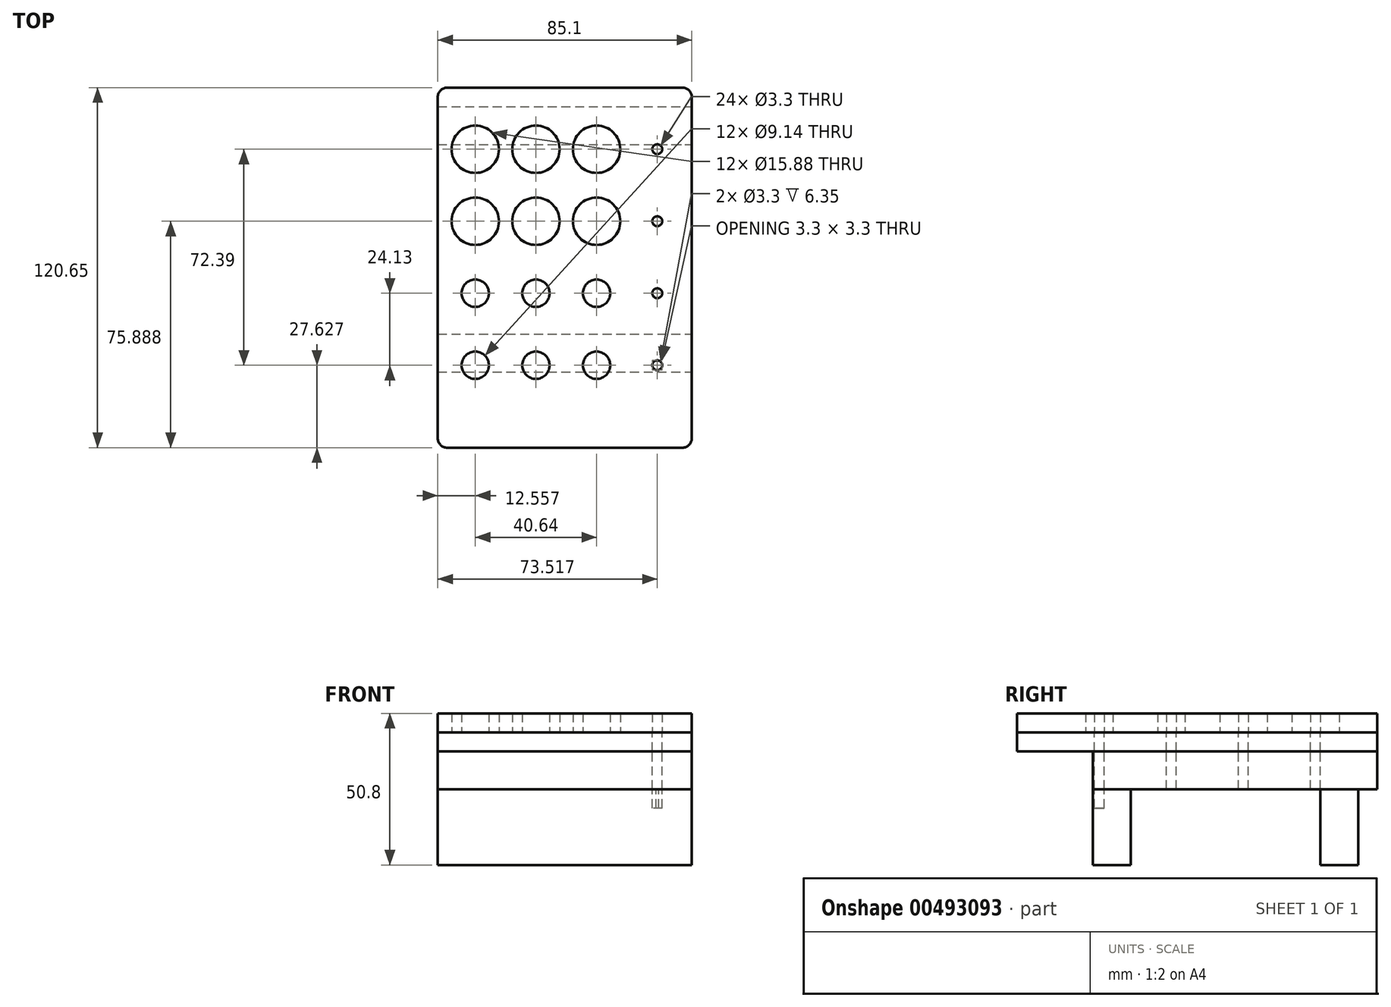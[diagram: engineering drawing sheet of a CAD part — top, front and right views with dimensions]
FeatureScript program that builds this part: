
annotation { "Feature Type Name" : "Feature", "Feature Type Description" : "" }
export const myFeature = defineFeature(function(context is Context, id is Id, definition is map)
    precondition{}
    {
        {
            var Q0;
            Q0=qCreatedBy(makeId("Top.planeOp"),FACE);
            var sketch = newSketch(context, id + "F0", { "sketchPlane" : qUnion([Q0])});
            skLineSegment(sketch, "E0.bottom", {"start": v(-42.55, 47.63) * mm, "end": v(42.55, 47.63) * mm});
            skLineSegment(sketch, "E0.top", {"start": v(-42.55, -47.63) * mm, "end": v(42.55, -47.63) * mm});
            skLineSegment(sketch, "E0.left", {"start": v(-42.55, 47.63) * mm, "end": v(-42.55, -47.63) * mm});
            skLineSegment(sketch, "E0.right", {"start": v(42.55, 47.63) * mm, "end": v(42.55, -47.63) * mm});
            skPoint(sketch, "E0.middle", {"position": v(0, 0) * mm});
            skSolve(sketch);
        }
        {
            var Q0;
            Q0=qSketchRegion(id+"F0",true);
            extrude(context, id + "F1", {"entities" : qUnion([Q0]), "depth" : 12.7 * mm});
        }
        {
            var Q0;
            Q0=makeQuery(id+"F1.opExtrude","CAP_FACE",FACE,{"disambiguationData":[OSD([sQuery(id+"F0.wireOp",EDGE,"E0.bottom"),sQuery(id+"F0.wireOp",EDGE,"E0.top"),sQuery(id+"F0.wireOp",EDGE,"E0.left"),sQuery(id+"F0.wireOp",EDGE,"E0.right")])],"isStart":false});
            var sketch = newSketch(context, id + "F2", { "sketchPlane" : qUnion([Q0])});
            skLineSegment(sketch, "E1", {"start": v(0, 47.63) * mm, "end": v(0, -47.63) * mm, "construction": true});
            skPoint(sketch, "E2", {"position": v(0, 41.28) * mm});
            skLineSegment(sketch, "E3.bottom", {"start": v(-42.55, 47.63) * mm, "end": v(42.55, 47.63) * mm});
            skLineSegment(sketch, "E3.top", {"start": v(-42.54, -73.03) * mm, "end": v(-36.2, -73.03) * mm});
            skLineSegment(sketch, "E3.left", {"start": v(-42.55, 47.62) * mm, "end": v(-42.55, -73.03) * mm});
            skLineSegment(sketch, "E3.right", {"start": v(42.55, 47.62) * mm, "end": v(42.55, -73.03) * mm});
            skLineSegment(sketch, "E4.trimOffspring", {"start": v(-21.97, -73.03) * mm, "end": v(-7.11, -73.03) * mm});
            skLineSegment(sketch, "E5.trimOffspring", {"start": v(7.11, -73.03) * mm, "end": v(21.97, -73.03) * mm});
            skLineSegment(sketch, "E6.trimOffspring", {"start": v(36.2, -73.03) * mm, "end": v(42.55, -73.03) * mm});
            skPoint(sketch, "E7.orphan", {"position": v(-36.2, -85.72) * mm});
            skPoint(sketch, "E8.MirrorCS.start.orphan", {"position": v(-21.97, -85.72) * mm});
            skPoint(sketch, "E9.orphan", {"position": v(7.11, -85.72) * mm});
            skPoint(sketch, "E10.top.start.orphan", {"position": v(21.97, -85.72) * mm});
            skPoint(sketch, "E11.orphan", {"position": v(36.2, -85.72) * mm});
            skLineSegment(sketch, "E12", {"start": v(-42.55, -73.03) * mm, "end": v(42.55, -73.03) * mm});
            skSolve(sketch);
        }
        {
            var Q0;
            Q0 = qSketchRegion(id + "F2", true);
            extrude(context, id + "F3", {"entities" : qUnion([Q0]), "depth" : 6.35 * mm});
        }
        {
            var Q0;
            Q0=makeQuery(id+"F1.opExtrude","CAP_FACE",FACE,{"disambiguationData":[OSD([sQuery(id+"F0.wireOp",EDGE,"E0.bottom"),sQuery(id+"F0.wireOp",EDGE,"E0.top"),sQuery(id+"F0.wireOp",EDGE,"E0.left"),sQuery(id+"F0.wireOp",EDGE,"E0.right")])],"isStart":true});
            var sketch = newSketch(context, id + "F4", { "sketchPlane" : qUnion([Q0])});
            skLineSegment(sketch, "E13.bottom", {"start": v(-42.55, 47.63) * mm, "end": v(42.55, 47.63) * mm});
            skLineSegment(sketch, "E13.top", {"start": v(-42.55, 34.93) * mm, "end": v(42.55, 34.93) * mm});
            skLineSegment(sketch, "E13.left", {"start": v(-42.55, 47.63) * mm, "end": v(-42.55, 34.93) * mm});
            skLineSegment(sketch, "E13.right", {"start": v(42.55, 47.63) * mm, "end": v(42.55, 34.93) * mm});
            skLineSegment(sketch, "E14.bottom", {"start": v(-42.55, -41.28) * mm, "end": v(42.55, -41.28) * mm});
            skLineSegment(sketch, "E14.top", {"start": v(-42.55, -28.58) * mm, "end": v(42.55, -28.58) * mm});
            skLineSegment(sketch, "E14.left", {"start": v(-42.55, -41.28) * mm, "end": v(-42.55, -28.58) * mm});
            skLineSegment(sketch, "E14.right", {"start": v(42.55, -41.28) * mm, "end": v(42.55, -28.58) * mm});
            skSolve(sketch);
        }
        {
            var Q0;
            Q0 = qSketchRegion(id + "F4", true);
            extrude(context, id + "F5", {"entities" : qUnion([Q0]), "depth" : 25.4 * mm});
        }
        {
            var Q0;
            Q0=makeQuery(id+"F3.opExtrude","CAP_FACE",FACE,{"disambiguationData":[OSD([sQuery(id+"F2.wireOp",EDGE,"E3.bottom"),sQuery(id+"F2.wireOp",EDGE,"E3.left"),sQuery(id+"F2.wireOp",EDGE,"E3.right"),sQuery(id+"F2.wireOp",EDGE,"E12")])],"isStart":false});
            var sketch = newSketch(context, id + "F6", { "sketchPlane" : qUnion([Q0])});
            skLineSegment(sketch, "E15.bottom", {"start": v(-42.55, 47.63) * mm, "end": v(42.55, 47.63) * mm});
            skLineSegment(sketch, "E15.top", {"start": v(-42.55, -73.03) * mm, "end": v(42.55, -73.03) * mm});
            skLineSegment(sketch, "E15.left", {"start": v(-42.55, 47.62) * mm, "end": v(-42.55, -73.03) * mm});
            skLineSegment(sketch, "E15.right", {"start": v(42.55, 47.62) * mm, "end": v(42.55, -73.03) * mm});
            skCircle(sketch, "E16", {"center": v(-30, 26.99) * mm, "radius": 7.94 * mm});
            skCircle(sketch, "E17.0.1.0", {"center": v(-30, 2.86) * mm, "radius": 7.94 * mm});
            skCircle(sketch, "E17.1.0.0", {"center": v(-9.67, 26.99) * mm, "radius": 7.94 * mm});
            skCircle(sketch, "E17.1.1.0", {"center": v(-9.67, 2.86) * mm, "radius": 7.94 * mm});
            skCircle(sketch, "E17.2.0.0", {"center": v(10.65, 26.99) * mm, "radius": 7.94 * mm});
            skCircle(sketch, "E17.2.1.0", {"center": v(10.65, 2.86) * mm, "radius": 7.94 * mm});
            skLineSegment(sketch, "E17.direction1", {"start": v(-30, 26.99) * mm, "end": v(-9.67, 26.99) * mm, "construction": true});
            skLineSegment(sketch, "E17.direction2", {"start": v(-30, 26.99) * mm, "end": v(-30, 2.86) * mm, "construction": true});
            skCircle(sketch, "E18.0.3.0", {"center": v(30.97, 26.99) * mm, "radius": 7.94 * mm, "construction": true});
            skCircle(sketch, "E18.0.3.1", {"center": v(30.97, 2.86) * mm, "radius": 7.94 * mm, "construction": true});
            skCircle(sketch, "E19", {"center": v(30.97, 26.99) * mm, "radius": 1.65 * mm});
            skCircle(sketch, "E20", {"center": v(30.97, 2.86) * mm, "radius": 1.65 * mm});
            skCircle(sketch, "E21.0.0.2", {"center": v(-30, -21.27) * mm, "radius": 7.94 * mm, "construction": true});
            skCircle(sketch, "E21.0.0.3", {"center": v(-30, -45.4) * mm, "radius": 7.94 * mm, "construction": true});
            skCircle(sketch, "E21.0.1.2", {"center": v(-9.67, -21.27) * mm, "radius": 7.94 * mm, "construction": true});
            skCircle(sketch, "E21.0.1.3", {"center": v(-9.67, -45.4) * mm, "radius": 7.94 * mm, "construction": true});
            skCircle(sketch, "E21.0.2.2", {"center": v(10.65, -21.27) * mm, "radius": 7.94 * mm, "construction": true});
            skCircle(sketch, "E21.0.2.3", {"center": v(10.65, -45.4) * mm, "radius": 7.94 * mm, "construction": true});
            skCircle(sketch, "E21.0.3.2", {"center": v(30.97, -21.27) * mm, "radius": 7.94 * mm, "construction": true});
            skCircle(sketch, "E21.0.3.3", {"center": v(30.97, -45.4) * mm, "radius": 7.94 * mm, "construction": true});
            skCircle(sketch, "E22", {"center": v(-30, -21.27) * mm, "radius": 4.57 * mm});
            skCircle(sketch, "E23", {"center": v(-9.67, -21.27) * mm, "radius": 4.57 * mm});
            skCircle(sketch, "E24", {"center": v(10.65, -21.27) * mm, "radius": 4.57 * mm});
            skCircle(sketch, "E25", {"center": v(30.97, -21.27) * mm, "radius": 1.65 * mm});
            skCircle(sketch, "E26", {"center": v(-30, -45.4) * mm, "radius": 4.57 * mm});
            skCircle(sketch, "E27", {"center": v(-9.67, -45.4) * mm, "radius": 4.57 * mm});
            skCircle(sketch, "E28", {"center": v(10.65, -45.4) * mm, "radius": 4.57 * mm});
            skCircle(sketch, "E29", {"center": v(30.97, -45.4) * mm, "radius": 1.65 * mm});
            skSolve(sketch);
        }
        {
            var Q0;
            Q0 = qSketchRegion(id + "F6", true);
            extrude(context, id + "F7", {"entities" : qUnion([Q0]), "depth" : 6.35 * mm});
        }
        {
            var Q0;
            Q0=makeQuery(id+"F3.opExtrude","CAP_FACE",FACE,{"disambiguationData":[OSD([sQuery(id+"F2.wireOp",EDGE,"E3.bottom"),sQuery(id+"F2.wireOp",EDGE,"E3.left"),sQuery(id+"F2.wireOp",EDGE,"E3.right"),sQuery(id+"F2.wireOp",EDGE,"E12")])],"isStart":false});
            var sketch = newSketch(context, id + "F8", { "sketchPlane" : qUnion([Q0])});
            skCircle(sketch, "E30.0", {"center": v(30.97, -45.4) * mm, "radius": 1.65 * mm});
            skCircle(sketch, "E31.0", {"center": v(30.97, -21.27) * mm, "radius": 1.65 * mm});
            skCircle(sketch, "E32.0", {"center": v(30.97, 2.86) * mm, "radius": 1.65 * mm});
            skCircle(sketch, "E33.0", {"center": v(30.97, 26.99) * mm, "radius": 1.65 * mm});
            skSolve(sketch);
        }
        {
            var Q0;
            Q0 = qSketchRegion(id + "F8", true);
            extrude(context, id + "F9", {"entities" : qUnion([Q0]), "operationType" : NewBodyOperationType.REMOVE, "oppositeDirection" : true, "depth" : 25.4 * mm});
        }
        {
            var Q0;
            Q0=makeQuery(id+"F7.opExtrude","SWEPT_EDGE",EDGE,{"disambiguationData":[OSD([sQuery(id+"F6.wireOp",EDGE,"E15.top"),sQuery(id+"F6.wireOp",EDGE,"E15.right")])]});
            var Q1;
            Q1=makeQuery(id+"F3.opExtrude","SWEPT_EDGE",EDGE,{"disambiguationData":[OSD([sQuery(id+"F2.wireOp",EDGE,"E3.right"),sQuery(id+"F2.wireOp",EDGE,"E12")])]});
            var Q2;
            Q2=makeQuery(id+"F7.opExtrude","SWEPT_EDGE",EDGE,{"disambiguationData":[OSD([sQuery(id+"F6.wireOp",EDGE,"E15.bottom"),sQuery(id+"F6.wireOp",EDGE,"E15.right")])]});
            var Q3;
            Q3=makeQuery(id+"F3.opExtrude","SWEPT_EDGE",EDGE,{"disambiguationData":[OSD([sQuery(id+"F2.wireOp",EDGE,"E3.bottom"),sQuery(id+"F2.wireOp",EDGE,"E3.right")])]});
            var Q4;
            Q4=makeQuery(id+"F1.opExtrude","SWEPT_EDGE",EDGE,{"disambiguationData":[OSD([sQuery(id+"F0.wireOp",EDGE,"E0.bottom"),sQuery(id+"F0.wireOp",EDGE,"E0.right")])]});
            var Q5;
            Q5=makeQuery(id+"F1.opExtrude","SWEPT_EDGE",EDGE,{"disambiguationData":[OSD([sQuery(id+"F0.wireOp",EDGE,"E0.bottom"),sQuery(id+"F0.wireOp",EDGE,"E0.left")])]});
            var Q6;
            Q6=makeQuery(id+"F3.opExtrude","SWEPT_EDGE",EDGE,{"disambiguationData":[OSD([sQuery(id+"F2.wireOp",EDGE,"E3.bottom"),sQuery(id+"F2.wireOp",EDGE,"E3.left")])]});
            var Q7;
            Q7=makeQuery(id+"F7.opExtrude","SWEPT_EDGE",EDGE,{"disambiguationData":[OSD([sQuery(id+"F6.wireOp",EDGE,"E15.top"),sQuery(id+"F6.wireOp",EDGE,"E15.left")])]});
            var Q8;
            Q8=makeQuery(id+"F3.opExtrude","SWEPT_EDGE",EDGE,{"disambiguationData":[OSD([sQuery(id+"F2.wireOp",EDGE,"E3.left"),sQuery(id+"F2.wireOp",EDGE,"E12")])]});
            var Q9;
            Q9=makeQuery(id+"F7.opExtrude","SWEPT_EDGE",EDGE,{"disambiguationData":[OSD([sQuery(id+"F6.wireOp",EDGE,"E15.bottom"),sQuery(id+"F6.wireOp",EDGE,"E15.left")])]});
            fillet(context, id + "F10", {"entities" : qUnion([Q0, Q1, Q2, Q3, Q4, Q5, Q6, Q7, Q8, Q9]), "radius" : 3.17 * mm, "tangentPropagation" : true, "allowEdgeOverflow" : false});
        }
    });
